# Revit family: 0045160 Sylvania Lighting Fixture LED IP20 BATTEN L1500 SINGLE 4000K
name_source: partatom
category: Lighting Fixtures
revit_build: Autodesk Revit 2017 (Build: 20190507_1515(x64)
units: mm (PartAtom-declared; Revit-internal decimal feet)

## family parameters
Cut with Voids When Loaded = No
Host = Face
Light Source = Yes
OmniClass Number = 23.80.70.00
OmniClass Title = Lighting
Part Type = Normal
Room Calculation Point = No
Round Connector Dimension = Use Diameter
Shared = No

## types (1)
- 0045160 LED IP20 BATTEN L1500 SINGLE 4000K
    Apparent Load = 18 VA
    Assembly Code = D5020200
    AssetType = Fixed
    ClassificationName = Uniclass2015
    ClassificationValue = EF_70_80
    Color Filter = 16777215
    Cost = 0 $
    Default Elevation = 1219 mm
    Description = full range of LED Battens to replace traditional T8 battens (600mm, 1200mm, 1500mm and 1800mm), ease of installation, 18W, 2200 lum, 4000K, 25000h lifethtime
    Dimming Lamp Color Temperature Shift = <None>
    DocumentationLiterature = http://www.sylvania-lighting.com
    DurationUnit = hours
    ElectricShockClassification = Class I
    Emit Shape Visible in Rendering = No
    Emit from Rectangle Length = 1376 mm  [stored 4.51444 ft]
    Emit from Rectangle Width = 28 mm  [stored 0.0918635 ft]
    ExpectedLife = 50000
    Height_SYL = 46 mm  [stored 0.150919 ft]
    IfcExportAs = IfcLightFixtureType
    IfcExportType = IfcLightFixtureType
    ImpactProtectionIndex = IK02
    IngressProtection = IP20
    InputNominalFrequency = 50/60 Hz
    InputVoltage = 220-240V~
    Keynote = 16500
    Lamp = LED
    LampColourRenderingIndex = 80
    LampColourTemperature = 4000 K
    LampNominalLuminous = 2200 lm
    LampsType = LED
    Length_SYL = 1500 mm  [stored 4.92126 ft]
    LuminousEfficacy = 122.2 lm/W
    Manufacturer = Feilo Sylvania
    ManufacturerName = Feilo Sylvania
    Material_1_FEILO = Body-Sylvania-IP20LEDBatten
    Material_2_FEILO = Tube-Sylvania-IP20LEDBatten
    Material_3_FEILO = <By Category>
    Material_4_FEILO = <By Category>
    Model = LED IP20 BATTEN L1500 SINGLE 4000K
    ModelNumber = 0045160
    ModelReference = LED IP20 BATTEN L1500 SINGLE 4000K
    Name = LED IP20 BATTEN L1500 SINGLE 4000K
    NominalDepth = 43 mm
    NominalHeight = 48 mm
    NominalLength = 1500 mm  [stored 4.92126 ft]
    Photometric Web File = 0045160.ies
    PowerConsumption = 18 W
    PowerFactor = 0
    RadiusRadius_SYL = 5 mm  [stored 0.0164042 ft]
    RadiusTubeSleeve_SYL = 15 mm  [stored 0.0492126 ft]
    RadiusTube_SYL = 14 mm  [stored 0.0459318 ft]
    Tilt Angle = -90.00°
    Twin_SYL = No
    Type Image = <None>
    TypeName = LED IP20 BATTEN L1500 SINGLE 4000K
    URL = http://www.sylvania-lighting.com
    VisibilitySingle_SYL = Yes
    VisibilityTwin_SYL = No
    Voltage = 230 V
    Weight = 12.0 kg
    Width_SYL = 37 mm  [stored 0.121391 ft]

note: [stored X ft] marks values corroborated as IEEE doubles in the binary element streams (Revit-internal decimal feet)

## geometry (parser evidence)
native form markers: Sweep x2
no freeform markers — native parametric forms only
